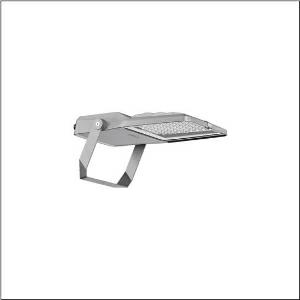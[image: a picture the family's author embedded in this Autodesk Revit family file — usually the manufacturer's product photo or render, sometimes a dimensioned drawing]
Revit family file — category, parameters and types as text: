
# Revit family: floodlight_fl_21_iq_mini___pl64_5xa7771c4e1a_d4bc
name_source: partatom
category: Lighting Fixtures
units: mm (PartAtom-declared; Revit-internal decimal feet)

## family parameters
Cut with Voids When Loaded = No
Host = Face
Light Source = No
Part Type = Normal
Room Calculation Point = No
Round Connector Dimension = Use Diameter
Shared = No

## types (1)
- --- (1 x LED, 12280 lm, 87.2 W, 4000K)
    Apparent Load = 87 VA
    CIE Flux Codes = 28 80 98 100 100
    Color Rendering = 70
    Color Temperature = 4000K
    Default Elevation = 1800 mm
    Description = Floodlight FL 21 iQ mini, floodlight, primary light control with lens, of PMMA, primary optical cover: protective disc, of toughened safety glass, transparent, light distribution: PL64, light emission: direct distribution, installation type: surface-mounted, LED, High Power LED, rated luminous flux: 12.280lm, luminous efficacy: 141lm/W, light colour: 740, colour temperature: 4000K, control gear: iQ Comfort/DALI, control: Auto-Match, Temp-Guard, Lumen-Switch, Night-Set, Smart-Wire, Light-Fading, Desk-Remote (wireless, voltage-free reading and setting of iQ features in the workshop via application-optimized NFC function/RFID function), optimised constant luminous flux control (CLO 2.0), with terminal, 6-pole, mains connection: 220..240V, AC, 50/60Hz, start of lifetime: 87W, end of service life: 92W, reduction: 40W, luminaire housing, of diecast aluminium, powder-coated, Siteco® metallic grey (DB 702S), corrosivity category C5 mid according to DIN EN ISO 12944, suitable for swimming pools, chlorine-resistant, sealing non-destructively replaceable, mounting bracket, of steel, galvanised, powder-coated, Siteco® metallic grey (DB 702S), protection rating (complete): IP66, insulation class (complete): insulation class II (safety insulation), certification: CE, ENEC, VDE, protection symbol: D, impact resistance: IK08, permissible operating ambient temperature: -40..+40°C, permissible operating ambient temperature for outdoor applications: -40..+50°C, standard: DIN EN 12944, LABS conformity tested according to VDMA 24364:2018-05, packaging unit: 1 piece

Light Distribution: PL64
    Height = 70 mm
    Lamp = 1 x LED
    Lamp Light Flux = 12280 lm
    Lamp Power = 87.2 W
    Lamp count = 1
    Length = 485 mm
    Luminous efficacy = 141 lm/W
    Manufacturer = Siteco
    ModVariant = No
    Model = 5XA7771C4E1A
    Number of Poles = 1
    OnlyDefault = Yes
    Power Factor = 1
    Product Name = Floodlight FL 21 iQ mini | PL64
    Product group = floodlight | pylon annexe
    ProductGroupID = 6200
    Protection Class = Protection class II
    Protection Degree = IP 66
    RLX_Detail_Level = 1
    RLX_Emergency_Light_Flux = 0 lm
    RLX_Emergency_Type = 0
    RLX_Emergency_Type_DB = No
    RlxData = <blob elided: 96361 chars, md5=5e087a4b>
    Socket = socket
    Standby Power = 0 W
    System Light Flux = 12280 lm
    System Power = 87 W
    Type Comments = factory setting: luminous flux: 100 % | dim-lin: 254 | 456 mA
    Type Image = l_1006845.jpg
    URL = http://relux.com
    VarID = @adj_166578
    Voltage = 0 V
    Weight = 0.00 kg
    Width = 337 mm

## geometry (parser evidence)
native form markers: Blend x4, Sweep x12
no freeform markers — native parametric forms only
